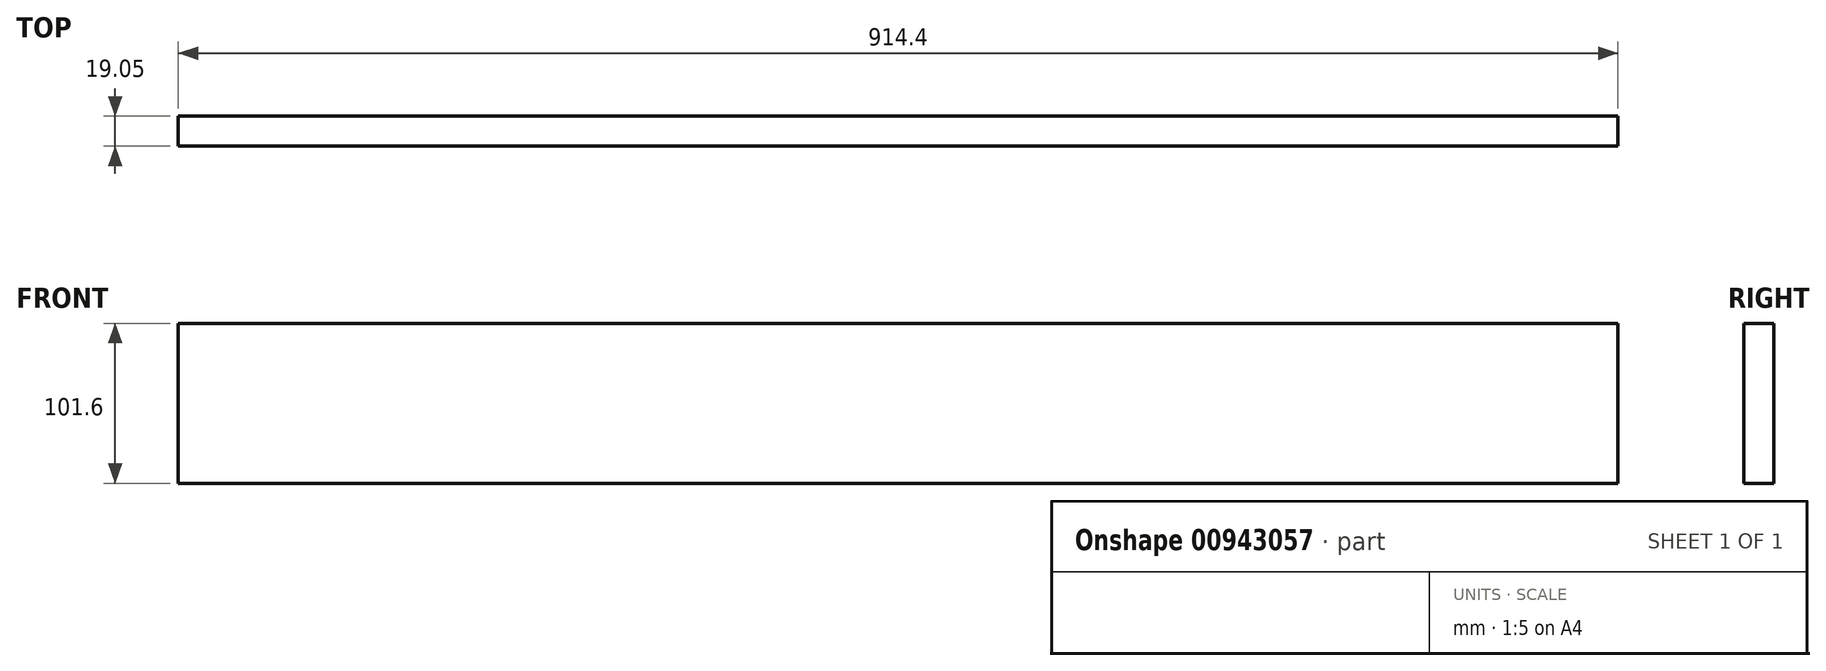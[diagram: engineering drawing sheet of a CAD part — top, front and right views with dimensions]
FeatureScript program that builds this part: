
annotation { "Feature Type Name" : "Feature", "Feature Type Description" : "" }
export const myFeature = defineFeature(function(context is Context, id is Id, definition is map)
    precondition{}
    {
        {
            var Q0;
            Q0=qCreatedBy(makeId("Front.planeOp"),FACE);
            var sketch = newSketch(context, id + "F0", { "sketchPlane" : qUnion([Q0])});
            skLineSegment(sketch, "E0.bottom", {"start": v(0, 0) * mm, "end": v(914.4, 0) * mm});
            skLineSegment(sketch, "E0.top", {"start": v(0, 101.6) * mm, "end": v(914.4, 101.6) * mm});
            skLineSegment(sketch, "E0.left", {"start": v(0, 0) * mm, "end": v(0, 101.6) * mm});
            skLineSegment(sketch, "E0.right", {"start": v(914.4, 0) * mm, "end": v(914.4, 101.6) * mm});
            skSolve(sketch);
        }
        {
            var Q0;
            Q0=makeQuery(id+"F0.imprint","IMPRINT",FACE,{"disambiguationData":[TD([[makeQuery(id+"F0.imprint","IMPRINT",EDGE,{"derivedFrom":sQuery(id+"F0.wireOp",EDGE,"E0.bottom")}),1.0]])]});
            extrude(context, id + "F1", {"entities" : qUnion([Q0]), "depth" : 19.05 * mm, "offsetDistance" : 25.4 * mm});
        }
    });
